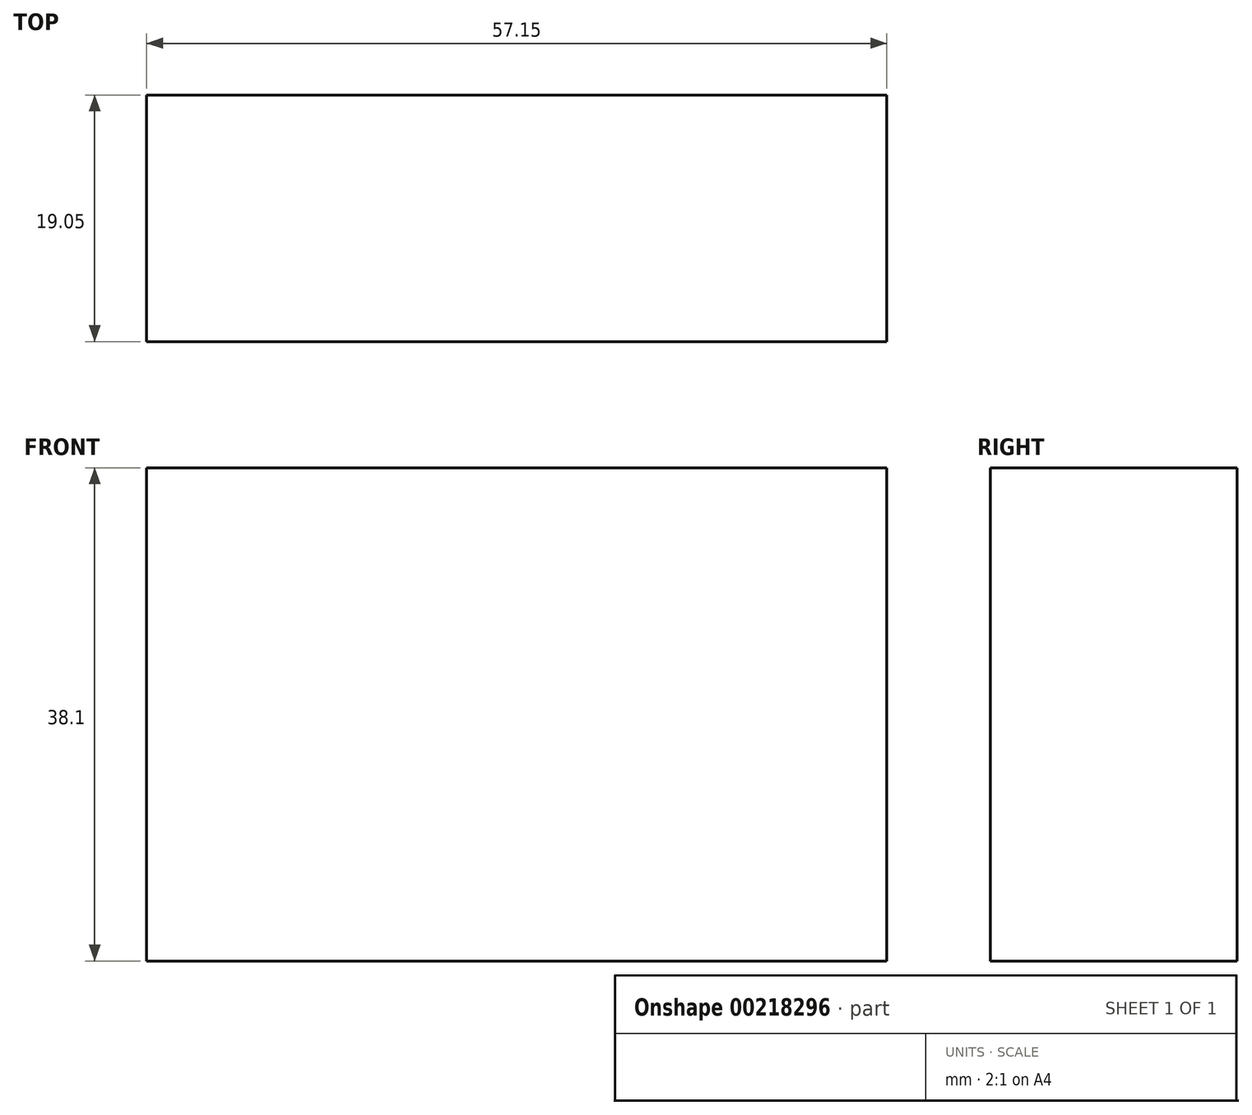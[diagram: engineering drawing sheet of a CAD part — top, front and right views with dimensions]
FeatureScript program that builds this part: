
annotation { "Feature Type Name" : "Feature", "Feature Type Description" : "" }
export const myFeature = defineFeature(function(context is Context, id is Id, definition is map)
    precondition{}
    {
        {
            var Q0;
            Q0=qCreatedBy(makeId("Front.planeOp"),FACE);
            var sketch = newSketch(context, id + "F0", { "sketchPlane" : qUnion([Q0])});
            skLineSegment(sketch, "E0", {"start": v(-48.08, -30.54) * mm, "end": v(-29.03, -30.54) * mm});
            skLineSegment(sketch, "E1", {"start": v(-29.03, -30.54) * mm, "end": v(-29.03, -11.5) * mm});
            skLineSegment(sketch, "E2", {"start": v(-29.03, -11.5) * mm, "end": v(-48.08, -11.5) * mm});
            skLineSegment(sketch, "E3", {"start": v(-48.08, -11.5) * mm, "end": v(-48.08, -30.54) * mm});
            skLineSegment(sketch, "E4", {"start": v(-29.03, -11.5) * mm, "end": v(-9.98, -11.5) * mm});
            skLineSegment(sketch, "E5", {"start": v(-9.98, -11.5) * mm, "end": v(-9.98, -30.54) * mm});
            skLineSegment(sketch, "E6", {"start": v(-9.98, -30.54) * mm, "end": v(-29.03, -30.54) * mm});
            skLineSegment(sketch, "E7", {"start": v(-9.98, -11.5) * mm, "end": v(9.07, -11.5) * mm});
            skLineSegment(sketch, "E8", {"start": v(9.07, -11.5) * mm, "end": v(9.07, -30.54) * mm});
            skLineSegment(sketch, "E9", {"start": v(9.07, -30.54) * mm, "end": v(-9.98, -30.54) * mm});
            skLineSegment(sketch, "E10", {"start": v(-48.08, -11.5) * mm, "end": v(-48.08, 7.56) * mm});
            skLineSegment(sketch, "E11", {"start": v(-48.08, 7.56) * mm, "end": v(9.07, 7.56) * mm});
            skLineSegment(sketch, "E12", {"start": v(9.07, 7.56) * mm, "end": v(9.07, -11.5) * mm});
            skLineSegment(sketch, "E13", {"start": v(-29.03, -11.5) * mm, "end": v(-29.03, 7.56) * mm});
            skLineSegment(sketch, "E14", {"start": v(-9.98, -11.5) * mm, "end": v(-9.98, 7.56) * mm});
            skSolve(sketch);
        }
        {
            var Q0;
            Q0=makeQuery(id+"F0.imprint","IMPRINT",FACE,{"disambiguationData":[TD([[makeQuery(id+"F0.imprint","IMPRINT",EDGE,{"derivedFrom":sQuery(id+"F0.wireOp",EDGE,"E2")}),-1.0]])]});
            var Q1;
            Q1=makeQuery(id+"F0.imprint","IMPRINT",FACE,{"disambiguationData":[TD([[makeQuery(id+"F0.imprint","IMPRINT",EDGE,{"derivedFrom":sQuery(id+"F0.wireOp",EDGE,"E4")}),1.0]])]});
            var Q2;
            Q2=makeQuery(id+"F0.imprint","IMPRINT",FACE,{"disambiguationData":[TD([[makeQuery(id+"F0.imprint","IMPRINT",EDGE,{"derivedFrom":sQuery(id+"F0.wireOp",EDGE,"E7")}),1.0]])]});
            var Q3;
            Q3=makeQuery(id+"F0.imprint","IMPRINT",FACE,{"disambiguationData":[TD([[makeQuery(id+"F0.imprint","IMPRINT",EDGE,{"derivedFrom":sQuery(id+"F0.wireOp",EDGE,"E5")}),1.0]])]});
            var Q4;
            Q4=makeQuery(id+"F0.imprint","IMPRINT",FACE,{"disambiguationData":[TD([[makeQuery(id+"F0.imprint","IMPRINT",EDGE,{"derivedFrom":sQuery(id+"F0.wireOp",EDGE,"E1")}),-1.0]])]});
            var Q5;
            Q5=makeQuery(id+"F0.imprint","IMPRINT",FACE,{"disambiguationData":[TD([[makeQuery(id+"F0.imprint","IMPRINT",EDGE,{"derivedFrom":sQuery(id+"F0.wireOp",EDGE,"E0")}),1.0]])]});
            extrude(context, id + "F1", {"entities" : qUnion([Q0, Q1, Q2, Q3, Q4, Q5]), "depth" : 19.05 * mm});
        }
    });
